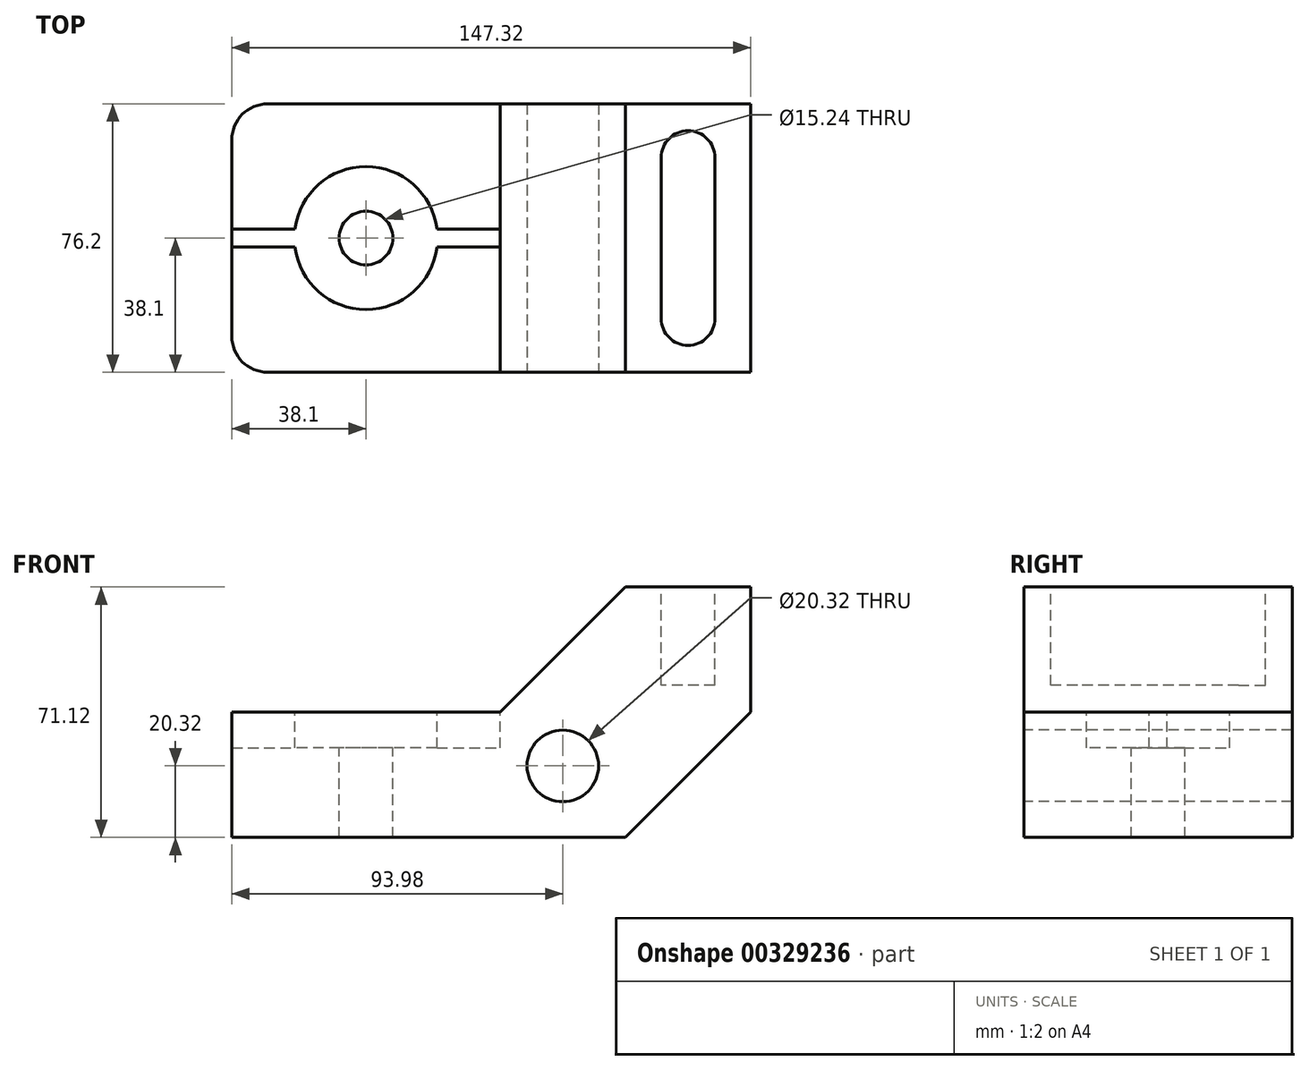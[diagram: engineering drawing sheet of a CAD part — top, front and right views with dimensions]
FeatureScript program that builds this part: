
annotation { "Feature Type Name" : "Feature", "Feature Type Description" : "" }
export const myFeature = defineFeature(function(context is Context, id is Id, definition is map)
    precondition{}
    {
        {
            var Q0;
            Q0=qCreatedBy(makeId("Front.planeOp"),FACE);
            var sketch = newSketch(context, id + "F0", { "sketchPlane" : qUnion([Q0])});
            skLineSegment(sketch, "E0", {"start": v(0, 0) * mm, "end": v(0, 35.56) * mm});
            skLineSegment(sketch, "E1", {"start": v(0, 35.56) * mm, "end": v(76.2, 35.56) * mm});
            skLineSegment(sketch, "E2", {"start": v(76.2, 35.56) * mm, "end": v(111.76, 71.12) * mm});
            skLineSegment(sketch, "E3", {"start": v(111.76, 71.12) * mm, "end": v(147.32, 71.12) * mm});
            skLineSegment(sketch, "E4", {"start": v(147.32, 71.12) * mm, "end": v(147.32, 35.56) * mm});
            skLineSegment(sketch, "E5", {"start": v(147.32, 35.56) * mm, "end": v(111.76, 0) * mm});
            skLineSegment(sketch, "E6", {"start": v(111.76, 0) * mm, "end": v(0, 0) * mm});
            skSolve(sketch);
        }
        {
            var Q0;
            Q0 = qSketchRegion(id + "F0", true);
            extrude(context, id + "F1", {"entities" : qUnion([Q0]), "depth" : 76.2 * mm});
        }
        {
            var Q0;
            Q0=makeQuery(id+"F1.opExtrude","CAP_EDGE",EDGE,{"disambiguationData":[OSD([sQuery(id+"F0.wireOp",EDGE,"E0")])],"isStart":true});
            var Q1;
            Q1=makeQuery(id+"F1.opExtrude","CAP_EDGE",EDGE,{"disambiguationData":[OSD([sQuery(id+"F0.wireOp",EDGE,"E0")])],"isStart":false});
            fillet(context, id + "F2", {"entities" : qUnion([Q0, Q1]), "radius" : 10.16 * mm, "tangentPropagation" : true, "allowEdgeOverflow" : false});
        }
        {
            var Q0;
            Q0=makeQuery(id+"F1.opExtrude","CAP_FACE",FACE,{"disambiguationData":[OSD([sQuery(id+"F0.wireOp",EDGE,"E0"),sQuery(id+"F0.wireOp",EDGE,"E1"),sQuery(id+"F0.wireOp",EDGE,"E2"),sQuery(id+"F0.wireOp",EDGE,"E3"),sQuery(id+"F0.wireOp",EDGE,"E4"),sQuery(id+"F0.wireOp",EDGE,"E5"),sQuery(id+"F0.wireOp",EDGE,"E6")])],"isStart":false});
            var sketch = newSketch(context, id + "F3", { "sketchPlane" : qUnion([Q0])});
            skCircle(sketch, "E7", {"center": v(93.98, 20.32) * mm, "radius": 10.16 * mm});
            skSolve(sketch);
        }
        {
            var Q0;
            Q0 = qSketchRegion(id + "F3", true);
            extrude(context, id + "F4", {"entities" : qUnion([Q0]), "operationType" : NewBodyOperationType.REMOVE, "endBound" : BoundingType.THROUGH_ALL, "oppositeDirection" : true, "depth" : 25.4 * mm});
        }
        {
            var Q0;
            Q0=makeQuery(id+"F1.opExtrude","SWEPT_FACE",FACE,{"disambiguationData":[OSD([sQuery(id+"F0.wireOp",EDGE,"E3")])]});
            var sketch = newSketch(context, id + "F5", { "sketchPlane" : qUnion([Q0])});
            skPoint(sketch, "E8", {"position": v(129.54, -15.24) * mm});
            skPoint(sketch, "E9", {"position": v(129.54, -60.96) * mm});
            skPoint(sketch, "E10", {"position": v(38.1, -38.1) * mm});
            skSolve(sketch);
        }
        {
            var Q0;
            Q0=sQuery(id+"F5.wireOp",VERTEX,"E10");
            var Q1;
            Q1=makeQuery(id+"F1.opExtrude","SWEPT_BODY",BODY,{"disambiguationData":[OSD([sQuery(id+"F0.wireOp",EDGE,"E0"),sQuery(id+"F0.wireOp",EDGE,"E1"),sQuery(id+"F0.wireOp",EDGE,"E2"),sQuery(id+"F0.wireOp",EDGE,"E3"),sQuery(id+"F0.wireOp",EDGE,"E4"),sQuery(id+"F0.wireOp",EDGE,"E5"),sQuery(id+"F0.wireOp",EDGE,"E6")])]});
            hole(context, id + "F6", {"style" : HoleStyle.C_BORE, "endStyle" : HoleEndStyle.THROUGH, "holeDiameter" : 15.24 * mm, "cBoreDiameter" : 40.64 * mm, "cBoreDepth" : 10.16 * mm, "tappedDepth" : 12.7 * mm, "tapClearance" : 3, "locations" : qUnion([Q0]), "scope" : qUnion([Q1])});
        }
        {
            var Q0;
            Q0=makeQuery(id+"F1.opExtrude","SWEPT_FACE",FACE,{"disambiguationData":[OSD([sQuery(id+"F0.wireOp",EDGE,"E3")])]});
            var sketch = newSketch(context, id + "F7", { "sketchPlane" : qUnion([Q0])});
            skArc(sketch, "E11", {"start": v(121.92, -15.24) * mm, "mid": v(129.54, -7.62) * mm, "end": v(137.16, -15.24) * mm});
            skArc(sketch, "E12", {"start": v(121.92, -60.96) * mm, "mid": v(129.54, -68.58) * mm, "end": v(137.16, -60.96) * mm});
            skLineSegment(sketch, "E13", {"start": v(121.92, -15.24) * mm, "end": v(121.92, -60.96) * mm});
            skLineSegment(sketch, "E14", {"start": v(137.16, -15.24) * mm, "end": v(137.16, -60.96) * mm});
            skSolve(sketch);
        }
        {
            var Q0;
            Q0 = qSketchRegion(id + "F7", true);
            extrude(context, id + "F8", {"entities" : qUnion([Q0]), "operationType" : NewBodyOperationType.REMOVE, "oppositeDirection" : true, "depth" : 27.94 * mm});
        }
        {
            var Q0;
            Q0=makeQuery(id+"F1.opExtrude","SWEPT_FACE",FACE,{"disambiguationData":[OSD([sQuery(id+"F0.wireOp",EDGE,"E1")])]});
            var sketch = newSketch(context, id + "F9", { "sketchPlane" : qUnion([Q0])});
            skLineSegment(sketch, "E15", {"start": v(-12.79, -38.1) * mm, "end": v(80.12, -38.1) * mm, "construction": true});
            skPoint(sketch, "E15.startSnap0", {"position": v(0, -38.1) * mm});
            skPoint(sketch, "E15.endSnap0", {"position": v(76.2, -38.1) * mm});
            skLineSegment(sketch, "E16", {"start": v(0, -38.1) * mm, "end": v(0, -35.56) * mm});
            skLineSegment(sketch, "E17", {"start": v(0, -35.56) * mm, "end": v(76.2, -35.56) * mm});
            skLineSegment(sketch, "E18", {"start": v(76.2, -35.56) * mm, "end": v(76.2, -38.1) * mm});
            skLineSegment(sketch, "E19.MirrorCS", {"start": v(0, -38.1) * mm, "end": v(0, -40.64) * mm});
            skLineSegment(sketch, "E20.MirrorCS", {"start": v(0, -40.64) * mm, "end": v(76.2, -40.64) * mm});
            skLineSegment(sketch, "E21.MirrorCS", {"start": v(76.2, -40.64) * mm, "end": v(76.2, -38.1) * mm});
            skSolve(sketch);
        }
        {
            var Q0;
            Q0 = qSketchRegion(id + "F9", true);
            extrude(context, id + "F10", {"entities" : qUnion([Q0]), "operationType" : NewBodyOperationType.REMOVE, "oppositeDirection" : true, "depth" : 10.16 * mm});
        }
    });
